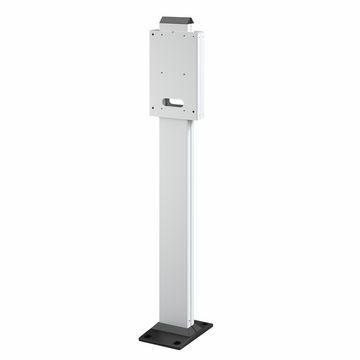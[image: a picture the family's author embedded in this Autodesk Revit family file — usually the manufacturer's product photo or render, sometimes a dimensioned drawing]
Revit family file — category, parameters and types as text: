
# Revit family: Building-RicaricaVeicoliElettrici-GEWISS-JOINON-ICON_SUPPORTO-PAVIM-BIFACC
name_source: partatom
category: Apparecchi elettrici
units: mm (PartAtom-declared; Revit-internal decimal feet)

## family parameters
Condiviso = No
Host = Superficie
Mantenere orientamento annotazione = Sì
Punto di calcolo locali = Sì
Quota connettore circolare = Usa diametro
Taglio con vuoti quando caricato = No
Tipo di parte = Normale

## types (1)
- GWJ8103 - SUPPORTO PAVIMENTO I-CON  BIFACCIALE
    Adatto per = WallBox I-CON
    BLOCCO = B=C
    Catalogo = E-MOBILITY
    Codice EAN = 8034035071386
    Codice Electrocod = 2242
    Descrizione = SUPPORTO PAVIMENTO I-CON  BIFACCIALE
    Descrizione: = Supporto pavimento I-CON - bifacciale
    FORMULA = 1000 mm  [stored 3.28084 ft]
    IDF = 8f4bcdbc-0f62-4252-8c45-9738275bca0f
    IDT = c8e419b7-85e3-4455-b847-1a1252f0ba31
    Immagine tipo = ICON_SUPP_BI.jpg
    L = 155 mm  [stored 0.50853 ft]
    Modello = GWJ8103
    N.poli = 1
    POMELLO = bianco
    PRESA = Giallo
    Produttore = GEWISS S.p.A.
    Prospetto di default = 1219 mm
    STRUTTURA = RAL - 7035
    STRUTTURA ALTA = blue
    Scheda Tecnica = https://www.gewiss.com
    Spostamento_S = 1500 mm  [stored 4.92126 ft]
    URL = https://www.gewiss.com
    VETRO = Vetro
    Versione file RFA = 19.4
    Voltaggio = 0 V
    W = 115 mm  [stored 0.377297 ft]

note: [stored X ft] marks values corroborated as IEEE doubles in the binary element streams (Revit-internal decimal feet)
